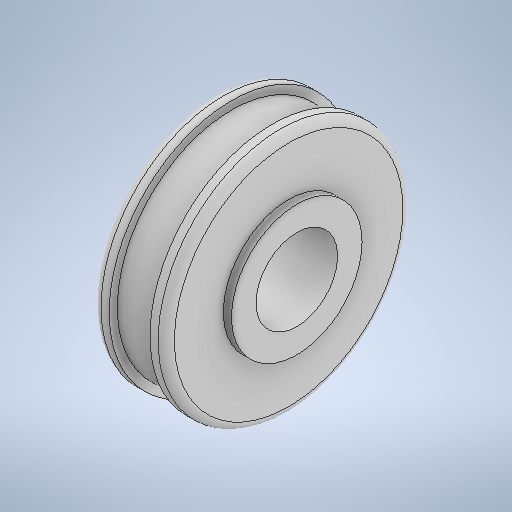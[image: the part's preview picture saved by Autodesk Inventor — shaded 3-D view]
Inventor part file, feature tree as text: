
AUTODESK INVENTOR PART (.ipt)
format: ipt  version: 2025.1 (Build 291241000, 241)  size: 323,072 bytes
history: native  units: mm
features: sketch x3, hole x2, revolve x1, fillet x1
ambient origin geometry x8: Origin, YZ Plane, XZ Plane, XY Plane, X Axis, Y Axis, Z Axis, Center Point
bodies: Solid1 (feature_tree)
feature tree (7):
  revolve  "Revolution1"  [1 undecoded]
  hole  "Hole2"  [1 undecoded]
  hole  "Hole3"  [1 undecoded]
  fillet  "Fillet2"  Radius=28.0mm
  sketch  "Sketch1"  dims[d0=30.0mm d1=2.0mm]
  sketch  "Sketch3"  dims[d2=2.0mm d3=9.0mm]
  sketch  "Sketch4"  dims[d4=16.0mm d5=1.0mm d6=28.0mm d7=90.0deg d15=4.134mm d16=10.0mm d17=4.0mm d18=2.0mm d19=90.0deg d20=10.0mm d21=0.0mm d23=10.0mm d24=9.0mm d25=4.0mm d26=2.0mm d27=90.0deg d28=9.0mm d29=0.0mm d30=1.0mm]
note: 3 required parameter values undecoded (feature->parameter linkage not recoverable at this tier; creation-order binding heuristic only, values carry confidence <= 0.55)